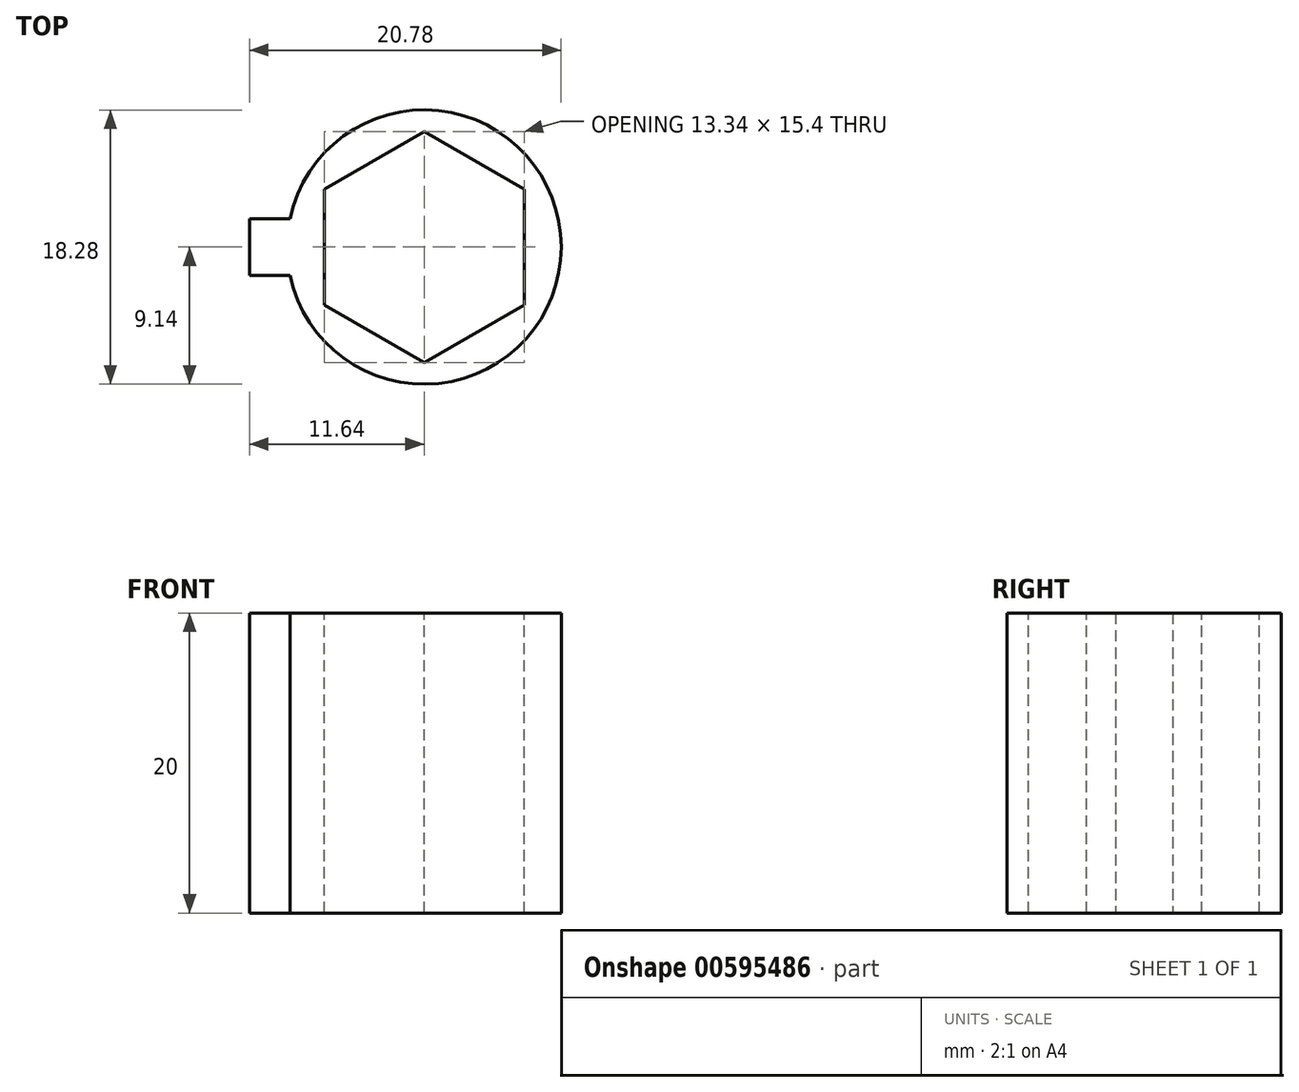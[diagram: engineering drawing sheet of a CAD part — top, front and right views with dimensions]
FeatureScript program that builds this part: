
annotation { "Feature Type Name" : "Feature", "Feature Type Description" : "" }
export const myFeature = defineFeature(function(context is Context, id is Id, definition is map)
    precondition{}
    {
        {
            var Q0;
            Q0=qCreatedBy(makeId("Top.planeOp"),FACE);
            var sketch = newSketch(context, id + "F0", { "sketchPlane" : qUnion([Q0])});
            skCircle(sketch, "E0", {"center": v(0, 0) * mm, "radius": 9.14 * mm});
            skLineSegment(sketch, "E1", {"start": v(0, 0) * mm, "end": v(0, -1.9) * mm});
            skLineSegment(sketch, "E2", {"start": v(0, -1.9) * mm, "end": v(-11.64, -1.9) * mm});
            skLineSegment(sketch, "E3", {"start": v(-11.64, -1.9) * mm, "end": v(-11.64, 1.9) * mm});
            skLineSegment(sketch, "E4", {"start": v(-11.64, 1.9) * mm, "end": v(0, 1.9) * mm});
            skLineSegment(sketch, "E5", {"start": v(0, 1.9) * mm, "end": v(0, 0.78) * mm});
            skPoint(sketch, "E5.endSnap0", {"position": v(0, -0.95) * mm});
            skSolve(sketch);
        }
        {
            var Q0;
            {var subQ0=sQuery(id+"F0.wireOp",EDGE,"E0");var subQ1=makeQuery(id+"F0.imprint","INTERSECT",VERTEX,{"derivedFrom":[subQ0,sQuery(id+"F0.wireOp",EDGE,"E2")]});Q0=makeQuery(id+"F0.imprint","IMPRINT",FACE,{"disambiguationData":[TD([[makeQuery(id+"F0.imprint","IMPRINT",EDGE,{"disambiguationData":[TD([[subQ1,1.0]])],"derivedFrom":subQ0}),1.0]])]});}
            var Q1;
            {var subQ5=sQuery(id+"F0.wireOp",EDGE,"E3");Q1=makeQuery(id+"F0.imprint","IMPRINT",FACE,{"disambiguationData":[TD([[makeQuery(id+"F0.imprint","IMPRINT",EDGE,{"derivedFrom":subQ5}),-1.0]])]});}
            extrude(context, id + "F1", {"entities" : qUnion([Q0, Q1]), "depth" : 20 * mm, "offsetDistance" : 25.4 * mm});
        }
        {
            var Q0;
            Q0=makeQuery(id+"F1.opExtrude","CAP_FACE",FACE,{"disambiguationData":[OSD([sQuery(id+"F0.wireOp",EDGE,"E0"),sQuery(id+"F0.wireOp",EDGE,"E2"),sQuery(id+"F0.wireOp",EDGE,"E3"),sQuery(id+"F0.wireOp",EDGE,"E4")])],"isStart":false});
            var sketch = newSketch(context, id + "F2", { "sketchPlane" : qUnion([Q0])});
            skCircle(sketch, "E6.cCircle", {"center": v(0, 0) * mm, "radius": 6.67 * mm, "construction": true});
            skLineSegment(sketch, "E6.0", {"start": v(6.67, 3.85) * mm, "end": v(6.67, -3.85) * mm});
            skLineSegment(sketch, "E6.1", {"start": v(6.67, -3.85) * mm, "end": v(0, -7.7) * mm});
            skLineSegment(sketch, "E6.2", {"start": v(0, -7.7) * mm, "end": v(-6.67, -3.85) * mm});
            skLineSegment(sketch, "E6.3", {"start": v(-6.67, -3.85) * mm, "end": v(-6.67, 3.85) * mm});
            skLineSegment(sketch, "E6.4", {"start": v(-6.67, 3.85) * mm, "end": v(0, 7.7) * mm});
            skLineSegment(sketch, "E6.5", {"start": v(0, 7.7) * mm, "end": v(6.67, 3.85) * mm});
            skPoint(sketch, "E6.0.midPoint", {"position": v(6.67, 0) * mm});
            skSolve(sketch);
        }
        {
            var Q0;
            Q0=makeQuery(id+"F2.imprint","IMPRINT",FACE,{"disambiguationData":[TD([[makeQuery(id+"F2.imprint","IMPRINT",EDGE,{"derivedFrom":sQuery(id+"F2.wireOp",EDGE,"E6.0")}),-1.0]])]});
            var Q1;
            Q1=makeQuery(id+"F1.opExtrude","CAP_FACE",FACE,{"disambiguationData":[OSD([sQuery(id+"F0.wireOp",EDGE,"E0"),sQuery(id+"F0.wireOp",EDGE,"E2"),sQuery(id+"F0.wireOp",EDGE,"E3"),sQuery(id+"F0.wireOp",EDGE,"E4")])],"isStart":true});
            extrude(context, id + "F3", {"entities" : qUnion([Q0]), "operationType" : NewBodyOperationType.REMOVE, "endBound" : BoundingType.UP_TO_SURFACE, "oppositeDirection" : true, "depth" : 25.4 * mm, "endBoundEntityFace" : qUnion([Q1]), "offsetDistance" : 25.4 * mm});
        }
    });
